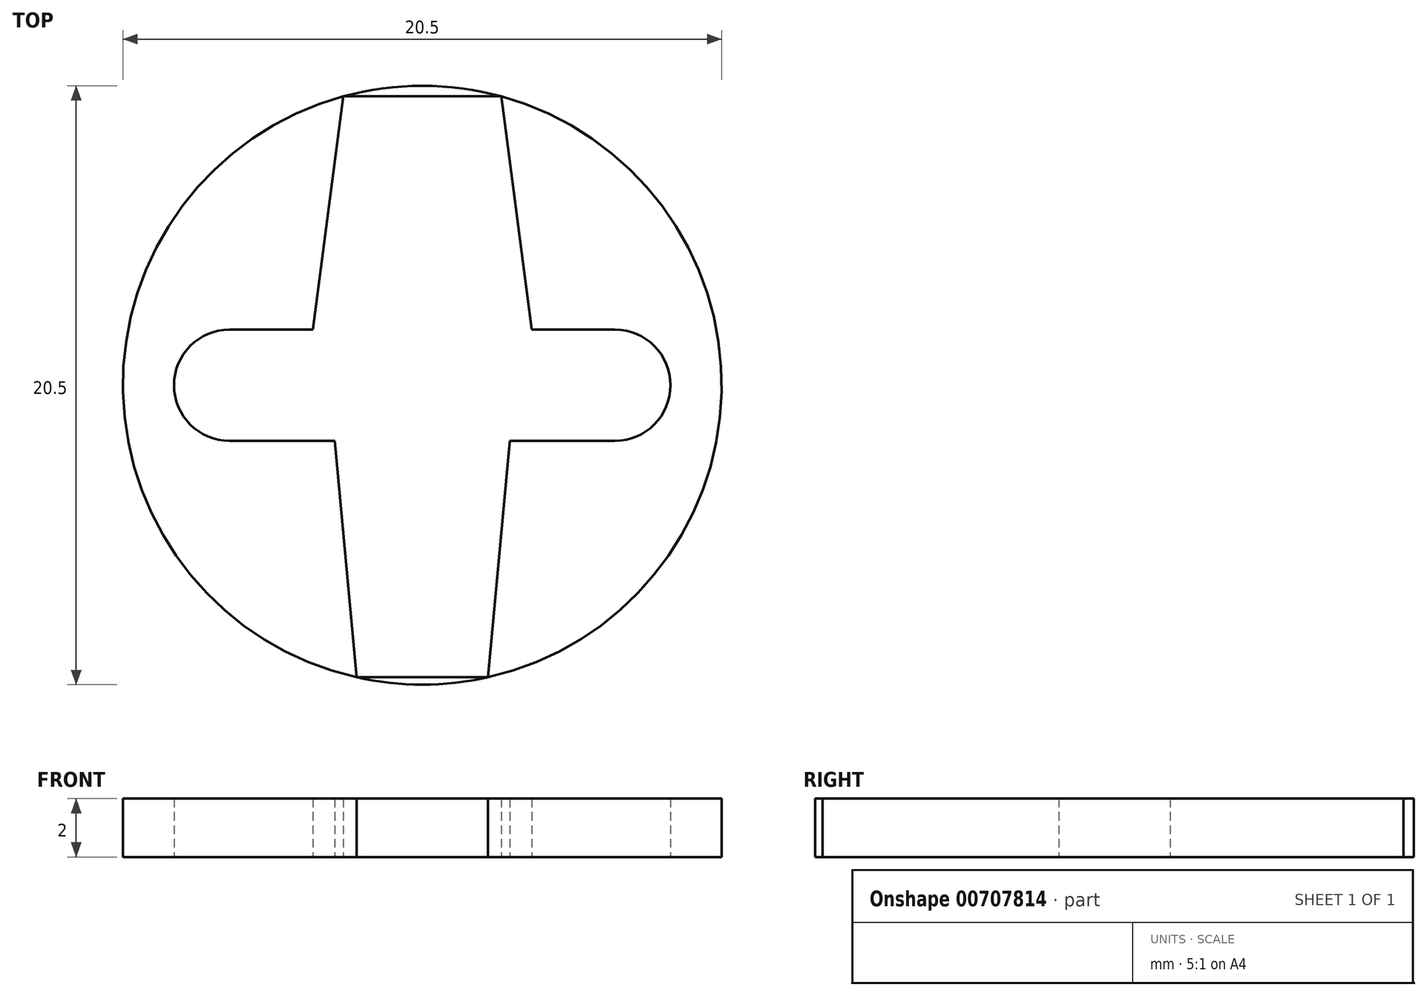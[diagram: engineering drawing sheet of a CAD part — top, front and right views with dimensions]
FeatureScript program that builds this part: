
annotation { "Feature Type Name" : "Feature", "Feature Type Description" : "" }
export const myFeature = defineFeature(function(context is Context, id is Id, definition is map)
    precondition{}
    {
        {
            var Q0;
            Q0=qCreatedBy(makeId("Top.planeOp"),FACE);
            var sketch = newSketch(context, id + "F0", { "sketchPlane" : qUnion([Q0])});
            skCircle(sketch, "E0", {"center": v(0, 0) * mm, "radius": 10.25 * mm});
            skLineSegment(sketch, "E1.bottom", {"start": v(-12.5, 12.5) * mm, "end": v(12.5, 12.5) * mm});
            skLineSegment(sketch, "E1.top", {"start": v(-12.5, -12.5) * mm, "end": v(12.5, -12.5) * mm});
            skLineSegment(sketch, "E1.left", {"start": v(-12.5, 12.5) * mm, "end": v(-12.5, -12.5) * mm});
            skLineSegment(sketch, "E1.right", {"start": v(12.5, 12.5) * mm, "end": v(12.5, -12.5) * mm});
            skLineSegment(sketch, "E2", {"start": v(0, 0) * mm, "end": v(-12.5, 12.5) * mm});
            skLineSegment(sketch, "E3", {"start": v(12.5, 12.5) * mm, "end": v(0, 0) * mm});
            skLineSegment(sketch, "E4", {"start": v(0, 0) * mm, "end": v(-12.5, -12.5) * mm});
            skLineSegment(sketch, "E5", {"start": v(0, 0) * mm, "end": v(12.5, -12.5) * mm});
            skLineSegment(sketch, "E6", {"start": v(-6.6, -1.9) * mm, "end": v(-1.9, -1.9) * mm});
            skLineSegment(sketch, "E7", {"start": v(-1.9, -1.9) * mm, "end": v(1.9, -1.9) * mm});
            skLineSegment(sketch, "E8", {"start": v(1.9, -1.9) * mm, "end": v(6.6, -1.9) * mm});
            skPoint(sketch, "E9", {"position": v(-6.6, 0) * mm});
            skPoint(sketch, "E10", {"position": v(6.6, 0) * mm});
            skCircle(sketch, "E11", {"center": v(-6.6, 0) * mm, "radius": 1.9 * mm});
            skCircle(sketch, "E12", {"center": v(6.6, 0) * mm, "radius": 1.9 * mm});
            skPoint(sketch, "E13", {"position": v(8.5, 0) * mm});
            skLineSegment(sketch, "E14", {"start": v(-6.6, 1.9) * mm, "end": v(6.6, 1.9) * mm});
            skLineSegment(sketch, "E15", {"start": v(6.6, 1.9) * mm, "end": v(6.6, -1.9) * mm});
            skLineSegment(sketch, "E16", {"start": v(-6.6, 1.9) * mm, "end": v(-6.6, -1.9) * mm});
            skPoint(sketch, "E17", {"position": v(-8.5, 0) * mm});
            skLineSegment(sketch, "E18", {"start": v(-6.6, 0) * mm, "end": v(0, 0) * mm});
            skLineSegment(sketch, "E19", {"start": v(6.6, 0) * mm, "end": v(0, 0) * mm});
            skLineSegment(sketch, "E20", {"start": v(-1.9, -1.9) * mm, "end": v(-1.9, 1.9) * mm});
            skLineSegment(sketch, "E21", {"start": v(-1.9, 1.9) * mm, "end": v(1.9, 1.9) * mm});
            skLineSegment(sketch, "E22", {"start": v(1.9, 1.9) * mm, "end": v(1.9, -1.9) * mm});
            skLineSegment(sketch, "E23", {"start": v(-3.75, 1.9) * mm, "end": v(-2.7, 9.89) * mm});
            skLineSegment(sketch, "E24", {"start": v(-2.7, 9.89) * mm, "end": v(2.7, 9.89) * mm});
            skLineSegment(sketch, "E25", {"start": v(2.7, 9.89) * mm, "end": v(3.75, 1.9) * mm});
            skLineSegment(sketch, "E26", {"start": v(-3.75, 1.9) * mm, "end": v(-1.9, 1.9) * mm});
            skLineSegment(sketch, "E27", {"start": v(1.9, 1.9) * mm, "end": v(3.75, 1.9) * mm});
            skLineSegment(sketch, "E28", {"start": v(-3, -1.9) * mm, "end": v(-2.25, -10) * mm});
            skLineSegment(sketch, "E29", {"start": v(-2.25, -10) * mm, "end": v(2.25, -10) * mm});
            skLineSegment(sketch, "E30", {"start": v(2.25, -10) * mm, "end": v(3, -1.9) * mm});
            skLineSegment(sketch, "E31", {"start": v(0, 0) * mm, "end": v(0, -10) * mm});
            skPoint(sketch, "E31.endSnap0", {"position": v(0, -12.5) * mm});
            skCircle(sketch, "E32", {"center": v(0, 0) * mm, "radius": 2.5 * mm});
            skSolve(sketch);
        }
        {
            var Q0;
            {var subQ1=sQuery(id+"F0.wireOp",EDGE,"E0");var subQ3=sQuery(id+"F0.wireOp",EDGE,"E5");var subQ4=makeQuery(id+"F0.imprint","INTERSECT",VERTEX,{"derivedFrom":[subQ1,subQ3]});Q0=makeQuery(id+"F0.imprint","IMPRINT",FACE,{"disambiguationData":[TD([[makeQuery(id+"F0.imprint","IMPRINT",EDGE,{"disambiguationData":[TD([[subQ4,1.0]])],"derivedFrom":subQ3}),-1.0]])]});}
            var Q1;
            {var subQ8=sQuery(id+"F0.wireOp",EDGE,"E0");var subQ10=sQuery(id+"F0.wireOp",EDGE,"E3");var subQ11=makeQuery(id+"F0.imprint","INTERSECT",VERTEX,{"derivedFrom":[subQ8,subQ10]});Q1=makeQuery(id+"F0.imprint","IMPRINT",FACE,{"disambiguationData":[TD([[makeQuery(id+"F0.imprint","IMPRINT",EDGE,{"disambiguationData":[TD([[subQ11,1.0]])],"derivedFrom":subQ8}),1.0]])]});}
            var Q2;
            {var subQ1=sQuery(id+"F0.wireOp",EDGE,"E0");var subQ3=sQuery(id+"F0.wireOp",EDGE,"E3");var subQ4=makeQuery(id+"F0.imprint","INTERSECT",VERTEX,{"derivedFrom":[subQ1,subQ3]});Q2=makeQuery(id+"F0.imprint","IMPRINT",FACE,{"disambiguationData":[TD([[makeQuery(id+"F0.imprint","IMPRINT",EDGE,{"disambiguationData":[TD([[subQ4,-1.0]])],"derivedFrom":subQ3}),-1.0]])]});}
            var Q3;
            {var subQ0=sQuery(id+"F0.wireOp",EDGE,"E24");Q3=makeQuery(id+"F0.imprint","IMPRINT",FACE,{"disambiguationData":[TD([[makeQuery(id+"F0.imprint","IMPRINT",EDGE,{"derivedFrom":subQ0}),1.0]])]});}
            var Q4;
            {var subQ1=sQuery(id+"F0.wireOp",EDGE,"E0");var subQ3=sQuery(id+"F0.wireOp",EDGE,"E2");var subQ4=makeQuery(id+"F0.imprint","INTERSECT",VERTEX,{"derivedFrom":[subQ1,subQ3]});Q4=makeQuery(id+"F0.imprint","IMPRINT",FACE,{"disambiguationData":[TD([[makeQuery(id+"F0.imprint","IMPRINT",EDGE,{"disambiguationData":[TD([[subQ4,1.0]])],"derivedFrom":subQ3}),-1.0]])]});}
            var Q5;
            {var subQ7=sQuery(id+"F0.wireOp",EDGE,"E0");var subQ10=sQuery(id+"F0.wireOp",EDGE,"E2");var subQ11=makeQuery(id+"F0.imprint","INTERSECT",VERTEX,{"derivedFrom":[subQ7,subQ10]});Q5=makeQuery(id+"F0.imprint","IMPRINT",FACE,{"disambiguationData":[TD([[makeQuery(id+"F0.imprint","IMPRINT",EDGE,{"disambiguationData":[TD([[subQ11,-1.0]])],"derivedFrom":subQ7}),1.0]])]});}
            var Q6;
            {var subQ1=sQuery(id+"F0.wireOp",EDGE,"E0");var subQ3=sQuery(id+"F0.wireOp",EDGE,"E4");var subQ4=makeQuery(id+"F0.imprint","INTERSECT",VERTEX,{"derivedFrom":[subQ1,subQ3]});Q6=makeQuery(id+"F0.imprint","IMPRINT",FACE,{"disambiguationData":[TD([[makeQuery(id+"F0.imprint","IMPRINT",EDGE,{"disambiguationData":[TD([[subQ4,1.0]])],"derivedFrom":subQ3}),1.0]])]});}
            var Q7;
            {var subQ0=sQuery(id+"F0.wireOp",EDGE,"E29");var subQ4=makeQuery(id+"F0.imprint","INTERSECT",VERTEX,{"derivedFrom":[subQ0,sQuery(id+"F0.wireOp",EDGE,"E31")]});Q7=makeQuery(id+"F0.imprint","IMPRINT",FACE,{"disambiguationData":[TD([[makeQuery(id+"F0.imprint","IMPRINT",EDGE,{"disambiguationData":[TD([[subQ4,1.0]])],"derivedFrom":subQ0}),-1.0]])]});}
            extrude(context, id + "F1", {"entities" : qUnion([Q0, Q1, Q2, Q3, Q4, Q5, Q6, Q7]), "depth" : 2 * mm, "offsetDistance" : 25 * mm});
        }
    });
